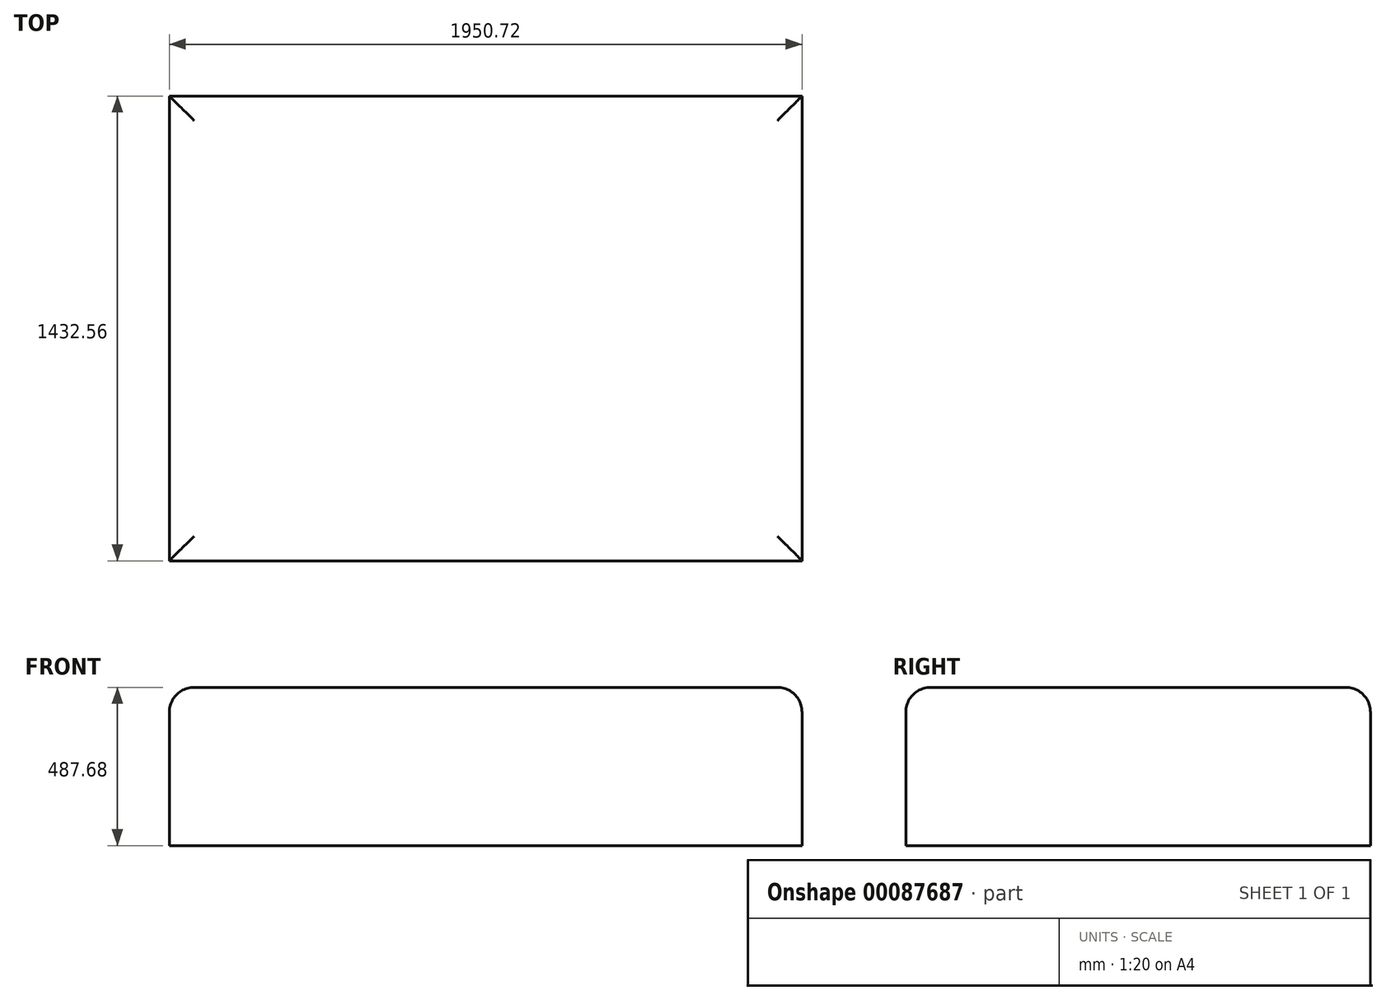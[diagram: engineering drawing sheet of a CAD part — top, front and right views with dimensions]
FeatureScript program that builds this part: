
annotation { "Feature Type Name" : "Feature", "Feature Type Description" : "" }
export const myFeature = defineFeature(function(context is Context, id is Id, definition is map)
    precondition{}
    {
        {
            var Q0;
            Q0=qCreatedBy(makeId("Top.planeOp"),FACE);
            var sketch = newSketch(context, id + "F0", { "sketchPlane" : qUnion([Q0])});
            skLineSegment(sketch, "E0.bottom", {"start": v(-741.42, 779.4) * mm, "end": v(1209.3, 779.4) * mm});
            skLineSegment(sketch, "E0.top", {"start": v(-741.42, -653.17) * mm, "end": v(1209.3, -653.17) * mm});
            skLineSegment(sketch, "E0.left", {"start": v(-741.42, 779.4) * mm, "end": v(-741.42, -653.17) * mm});
            skLineSegment(sketch, "E0.right", {"start": v(1209.3, 779.4) * mm, "end": v(1209.3, -653.17) * mm});
            skSolve(sketch);
        }
        {
            var Q0;
            Q0 = qSketchRegion(id + "F0", true);
            extrude(context, id + "F1", {"entities" : qUnion([Q0]), "depth" : 487.68 * mm});
        }
        {
            var Q0;
            Q0=makeQuery(id+"F1.opExtrude","CAP_FACE",FACE,{"disambiguationData":[OSD([sQuery(id+"F0.wireOp",EDGE,"E0.bottom"),sQuery(id+"F0.wireOp",EDGE,"E0.top"),sQuery(id+"F0.wireOp",EDGE,"E0.left"),sQuery(id+"F0.wireOp",EDGE,"E0.right")])],"isStart":false});
            fillet(context, id + "F2", {"entities" : qUnion([Q0]), "radius" : 76.2 * mm, "tangentPropagation" : true, "allowEdgeOverflow" : false});
        }
    });
